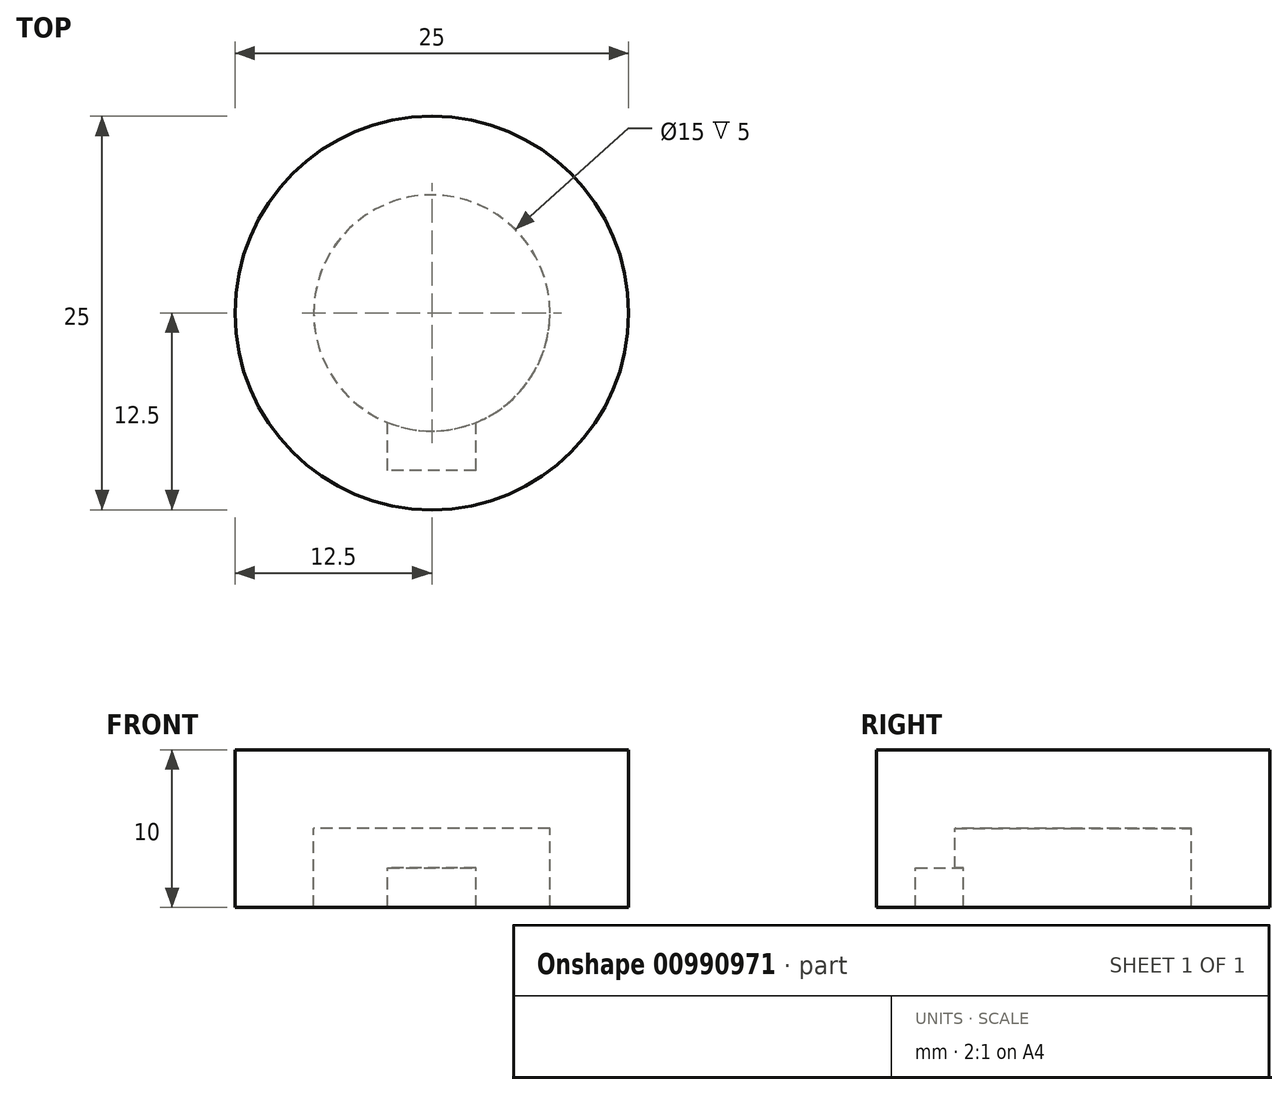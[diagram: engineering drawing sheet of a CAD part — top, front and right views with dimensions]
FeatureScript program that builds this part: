
annotation { "Feature Type Name" : "Feature", "Feature Type Description" : "" }
export const myFeature = defineFeature(function(context is Context, id is Id, definition is map)
    precondition{}
    {
        {
            var Q0;
            Q0=qCreatedBy(makeId("Top.planeOp"),FACE);
            var sketch = newSketch(context, id + "F0", { "sketchPlane" : qUnion([Q0])});
            skCircle(sketch, "E0", {"center": v(0, 0) * mm, "radius": 7.5 * mm});
            skCircle(sketch, "E1", {"center": v(0, 0) * mm, "radius": 12.5 * mm});
            skLineSegment(sketch, "E2", {"start": v(0, 0) * mm, "end": v(0, -13.85) * mm, "construction": true});
            skLineSegment(sketch, "E3", {"start": v(0, -10) * mm, "end": v(-2.8, -10) * mm});
            skLineSegment(sketch, "E4", {"start": v(-2.8, -10) * mm, "end": v(-2.8, -6.96) * mm});
            skLineSegment(sketch, "E5.MirrorCS", {"start": v(2.8, -10) * mm, "end": v(2.8, -6.96) * mm});
            skLineSegment(sketch, "E6.MirrorCS", {"start": v(0, -10) * mm, "end": v(2.8, -10) * mm});
            skPoint(sketch, "E7", {"position": v(0, -7.5) * mm});
            skPoint(sketch, "E7.positionSnap0", {"position": v(0, -6.92) * mm});
            skSolve(sketch);
        }
        {
            var Q0;
            {var subQ0=sQuery(id+"F0.wireOp",EDGE,"E0");var subQ1=makeQuery(id+"F0.imprint","INTERSECT",VERTEX,{"derivedFrom":[subQ0,sQuery(id+"F0.wireOp",EDGE,"E4")]});Q0=makeQuery(id+"F0.imprint","IMPRINT",FACE,{"disambiguationData":[TD([[makeQuery(id+"F0.imprint","IMPRINT",EDGE,{"disambiguationData":[TD([[subQ1,-1.0]])],"derivedFrom":subQ0}),1.0]])]});}
            var Q1;
            Q1=makeQuery(id+"F0.imprint","IMPRINT",FACE,{"disambiguationData":[TD([[makeQuery(id+"F0.imprint","IMPRINT",EDGE,{"derivedFrom":sQuery(id+"F0.wireOp",EDGE,"E3")}),-1.0]])]});
            var Q2;
            Q2=makeQuery(id+"F0.imprint","IMPRINT",FACE,{"disambiguationData":[TD([[makeQuery(id+"F0.imprint","IMPRINT",EDGE,{"derivedFrom":sQuery(id+"F0.wireOp",EDGE,"E1")}),1.0]])]});
            extrude(context, id + "F1", {"entities" : qUnion([Q0, Q1, Q2]), "endBound" : BoundingType.SYMMETRIC, "depth" : 10 * mm, "offsetDistance" : 25 * mm});
        }
        {
            var Q0;
            Q0=makeQuery(id+"F0.imprint","IMPRINT",FACE,{"disambiguationData":[TD([[makeQuery(id+"F0.imprint","IMPRINT",EDGE,{"derivedFrom":sQuery(id+"F0.wireOp",EDGE,"E3")}),-1.0]])]});
            var Q1;
            {var subQ0=sQuery(id+"F0.wireOp",EDGE,"E0");var subQ1=makeQuery(id+"F0.imprint","INTERSECT",VERTEX,{"derivedFrom":[subQ0,sQuery(id+"F0.wireOp",EDGE,"E4")]});Q1=makeQuery(id+"F0.imprint","IMPRINT",FACE,{"disambiguationData":[TD([[makeQuery(id+"F0.imprint","IMPRINT",EDGE,{"disambiguationData":[TD([[subQ1,-1.0]])],"derivedFrom":subQ0}),1.0]])]});}
            extrude(context, id + "F2", {"entities" : qUnion([Q0, Q1]), "operationType" : NewBodyOperationType.REMOVE, "endBound" : BoundingType.THROUGH_ALL, "oppositeDirection" : true, "depth" : 25 * mm, "offsetDistance" : 25 * mm});
        }
        {
            var Q0;
            Q0=makeQuery(id+"F0.imprint","IMPRINT",FACE,{"disambiguationData":[TD([[makeQuery(id+"F0.imprint","IMPRINT",EDGE,{"derivedFrom":sQuery(id+"F0.wireOp",EDGE,"E3")}),-1.0]])]});
            extrude(context, id + "F3", {"entities" : qUnion([Q0]), "operationType" : NewBodyOperationType.ADD, "oppositeDirection" : true, "depth" : 2.5 * mm, "offsetDistance" : 25 * mm});
        }
    });
